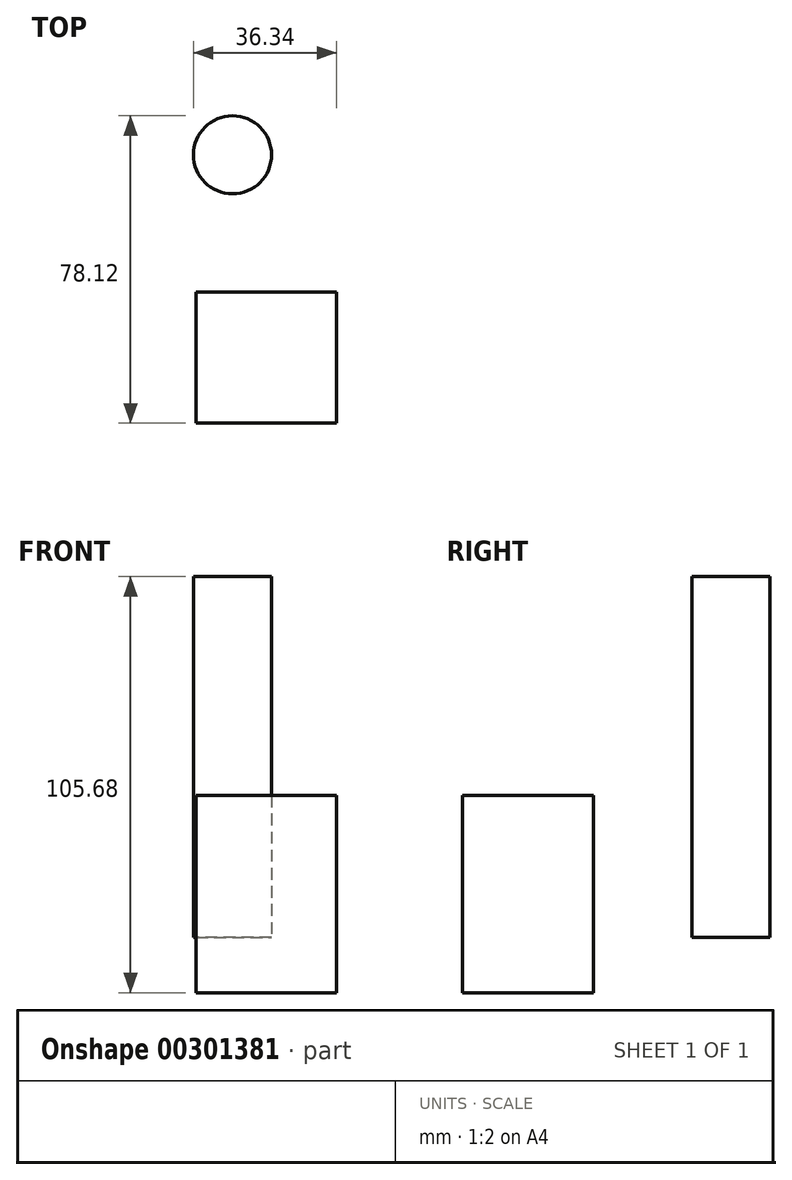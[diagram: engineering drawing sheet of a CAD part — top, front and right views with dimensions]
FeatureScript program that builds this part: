
annotation { "Feature Type Name" : "Feature", "Feature Type Description" : "" }
export const myFeature = defineFeature(function(context is Context, id is Id, definition is map)
    precondition{}
    {
        {
            var Q0;
            Q0=qCreatedBy(makeId("Top.planeOp"),FACE);
            var sketch = newSketch(context, id + "F0", { "sketchPlane" : qUnion([Q0])});
            skCircle(sketch, "E0", {"center": v(-43.44, 34.94) * mm, "radius": 9.92 * mm});
            skSolve(sketch);
        }
        {
            var Q0;
            Q0=makeQuery(id+"F0.imprint","IMPRINT",FACE,{"disambiguationData":[TD([[makeQuery(id+"F0.imprint","IMPRINT",EDGE,{"derivedFrom":sQuery(id+"F0.wireOp",EDGE,"E0")}),1.0]])]});
            extrude(context, id + "F1", {"entities" : qUnion([Q0]), "depth" : 54.36 * mm});
        }
        {
            var Q0;
            Q0=makeQuery(id+"F1.opExtrude","CAP_FACE",FACE,{"disambiguationData":[OSD([sQuery(id+"F0.wireOp",EDGE,"E0")])],"isStart":false});
            extrude(context, id + "F2", {"entities" : qUnion([Q0]), "operationType" : NewBodyOperationType.ADD, "depth" : 37.34 * mm});
        }
        {
            var Q0;
            Q0=qCreatedBy(makeId("Front.planeOp"),FACE);
            var sketch = newSketch(context, id + "F3", { "sketchPlane" : qUnion([Q0])});
            skLineSegment(sketch, "E1.bottom", {"start": v(-52.68, 36.1) * mm, "end": v(-17.02, 36.1) * mm});
            skLineSegment(sketch, "E1.top", {"start": v(-52.68, -14) * mm, "end": v(-17.02, -14) * mm});
            skLineSegment(sketch, "E1.left", {"start": v(-52.68, 36.1) * mm, "end": v(-52.68, -14) * mm});
            skLineSegment(sketch, "E1.right", {"start": v(-17.02, 36.1) * mm, "end": v(-17.02, -14) * mm});
            skSolve(sketch);
        }
        {
            var Q0;
            Q0=makeQuery(id+"F3.imprint","IMPRINT",FACE,{"disambiguationData":[TD([[makeQuery(id+"F3.imprint","IMPRINT",EDGE,{"derivedFrom":sQuery(id+"F3.wireOp",EDGE,"E1.bottom")}),-1.0]])]});
            extrude(context, id + "F4", {"entities" : qUnion([Q0]), "depth" : 33.27 * mm});
        }
    });
